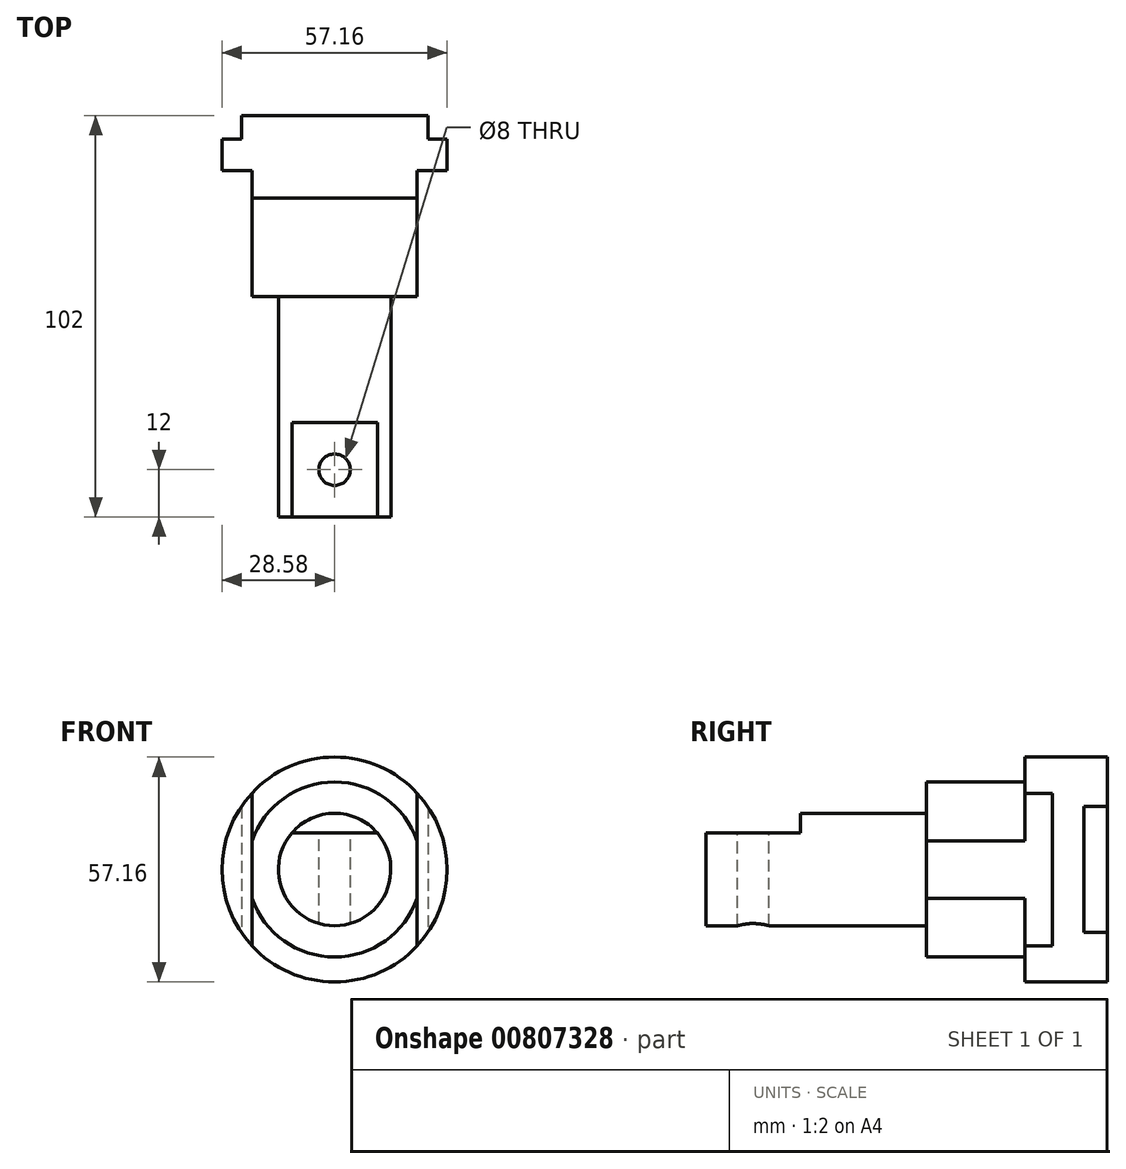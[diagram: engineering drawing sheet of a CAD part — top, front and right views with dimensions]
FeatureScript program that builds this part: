
annotation { "Feature Type Name" : "Feature", "Feature Type Description" : "" }
export const myFeature = defineFeature(function(context is Context, id is Id, definition is map)
    precondition{}
    {
        {
            var Q0;
            Q0=qCreatedBy(makeId("Front.planeOp"),FACE);
            var sketch = newSketch(context, id + "F0", { "sketchPlane" : qUnion([Q0])});
            skCircle(sketch, "E0", {"center": v(0, 0) * mm, "radius": 28.57 * mm});
            skCircle(sketch, "E1", {"center": v(0, 0) * mm, "radius": 22.23 * mm});
            skCircle(sketch, "E2", {"center": v(0, 0) * mm, "radius": 14.29 * mm});
            skLineSegment(sketch, "E3", {"start": v(-23.68, 16) * mm, "end": v(-23.68, -16) * mm});
            skLineSegment(sketch, "E4", {"start": v(0, 28.57) * mm, "end": v(0, -28.57) * mm, "construction": true});
            skLineSegment(sketch, "E5", {"start": v(28.57, 0) * mm, "end": v(-28.57, 0) * mm, "construction": true});
            skPoint(sketch, "E5.endSnap0", {"position": v(-23.68, 0) * mm});
            skLineSegment(sketch, "E6", {"start": v(-21, 19.38) * mm, "end": v(-21, -19.38) * mm});
            skLineSegment(sketch, "E7", {"start": v(-10.86, 9.29) * mm, "end": v(10.86, 9.29) * mm});
            skLineSegment(sketch, "E8.MirrorCS", {"start": v(23.68, 16) * mm, "end": v(23.68, -16) * mm});
            skLineSegment(sketch, "E9.MirrorCS", {"start": v(21, 19.38) * mm, "end": v(21, -19.38) * mm});
            skSolve(sketch);
        }
        {
            var Q0;
            {var subQ0=sQuery(id+"F0.wireOp",EDGE,"E3");Q0=makeQuery(id+"F0.imprint","IMPRINT",FACE,{"disambiguationData":[TD([[makeQuery(id+"F0.imprint","IMPRINT",EDGE,{"derivedFrom":subQ0}),1.0]])]});}
            var Q1;
            {var subQ0=sQuery(id+"F0.wireOp",EDGE,"E6");var subQ1=sQuery(id+"F0.wireOp",EDGE,"E1");var subQ2=makeQuery(id+"F0.imprint","INTERSECT",VERTEX,{"disambiguationData":[OD(0.0)],"derivedFrom":[subQ1,subQ0]});Q1=makeQuery(id+"F0.imprint","IMPRINT",FACE,{"disambiguationData":[TD([[makeQuery(id+"F0.imprint","IMPRINT",EDGE,{"disambiguationData":[TD([[subQ2,-1.0]])],"derivedFrom":subQ1}),1.0]])]});}
            var Q2;
            {var subQ0=sQuery(id+"F0.wireOp",EDGE,"E6");var subQ1=sQuery(id+"F0.wireOp",EDGE,"E0");var subQ2=makeQuery(id+"F0.imprint","INTERSECT",VERTEX,{"disambiguationData":[OD(0.0)],"derivedFrom":[subQ1,subQ0]});Q2=makeQuery(id+"F0.imprint","IMPRINT",FACE,{"disambiguationData":[TD([[makeQuery(id+"F0.imprint","IMPRINT",EDGE,{"disambiguationData":[TD([[subQ2,1.0]])],"derivedFrom":subQ1}),1.0]])]});}
            var Q3;
            {var subQ4=sQuery(id+"F0.wireOp",EDGE,"E6");var subQ5=sQuery(id+"F0.wireOp",EDGE,"E1");var subQ10=makeQuery(id+"F0.imprint","INTERSECT",VERTEX,{"disambiguationData":[OD(0.0)],"derivedFrom":[subQ5,subQ4]});Q3=makeQuery(id+"F0.imprint","IMPRINT",FACE,{"disambiguationData":[TD([[makeQuery(id+"F0.imprint","IMPRINT",EDGE,{"disambiguationData":[TD([[subQ10,1.0]])],"derivedFrom":subQ5}),1.0]])]});}
            var Q4;
            {var subQ0=sQuery(id+"F0.wireOp",EDGE,"E6");var subQ1=sQuery(id+"F0.wireOp",EDGE,"E0");var subQ2=makeQuery(id+"F0.imprint","INTERSECT",VERTEX,{"disambiguationData":[OD(1.0)],"derivedFrom":[subQ1,subQ0]});Q4=makeQuery(id+"F0.imprint","IMPRINT",FACE,{"disambiguationData":[TD([[makeQuery(id+"F0.imprint","IMPRINT",EDGE,{"disambiguationData":[TD([[subQ2,-1.0]])],"derivedFrom":subQ1}),1.0]])]});}
            var Q5;
            {var subQ0=sQuery(id+"F0.wireOp",EDGE,"E9.MirrorCS");var subQ1=sQuery(id+"F0.wireOp",EDGE,"E1");var subQ2=makeQuery(id+"F0.imprint","INTERSECT",VERTEX,{"disambiguationData":[OD(0.0)],"derivedFrom":[subQ1,subQ0]});Q5=makeQuery(id+"F0.imprint","IMPRINT",FACE,{"disambiguationData":[TD([[makeQuery(id+"F0.imprint","IMPRINT",EDGE,{"disambiguationData":[TD([[subQ2,1.0]])],"derivedFrom":subQ1}),1.0]])]});}
            var Q6;
            {var subQ0=sQuery(id+"F0.wireOp",EDGE,"E8.MirrorCS");Q6=makeQuery(id+"F0.imprint","IMPRINT",FACE,{"disambiguationData":[TD([[makeQuery(id+"F0.imprint","IMPRINT",EDGE,{"derivedFrom":subQ0}),-1.0]])]});}
            var Q7;
            {var subQ0=sQuery(id+"F0.wireOp",EDGE,"E7");Q7=makeQuery(id+"F0.imprint","IMPRINT",FACE,{"disambiguationData":[TD([[makeQuery(id+"F0.imprint","IMPRINT",EDGE,{"derivedFrom":subQ0}),-1.0]])]});}
            var Q8;
            {var subQ0=sQuery(id+"F0.wireOp",EDGE,"E7");Q8=makeQuery(id+"F0.imprint","IMPRINT",FACE,{"disambiguationData":[TD([[makeQuery(id+"F0.imprint","IMPRINT",EDGE,{"derivedFrom":subQ0}),1.0]])]});}
            extrude(context, id + "F1", {"entities" : qUnion([Q0, Q1, Q2, Q3, Q4, Q5, Q6, Q7, Q8]), "oppositeDirection" : true, "depth" : 6 * mm, "offsetDistance" : 25 * mm});
        }
        {
            var Q0;
            {var subQ0=sQuery(id+"F0.wireOp",EDGE,"E7");Q0=makeQuery(id+"F0.imprint","IMPRINT",FACE,{"disambiguationData":[TD([[makeQuery(id+"F0.imprint","IMPRINT",EDGE,{"derivedFrom":subQ0}),-1.0]])]});}
            var Q1;
            {var subQ0=sQuery(id+"F0.wireOp",EDGE,"E6");var subQ1=sQuery(id+"F0.wireOp",EDGE,"E1");var subQ2=makeQuery(id+"F0.imprint","INTERSECT",VERTEX,{"disambiguationData":[OD(0.0)],"derivedFrom":[subQ1,subQ0]});Q1=makeQuery(id+"F0.imprint","IMPRINT",FACE,{"disambiguationData":[TD([[makeQuery(id+"F0.imprint","IMPRINT",EDGE,{"disambiguationData":[TD([[subQ2,-1.0]])],"derivedFrom":subQ1}),1.0]])]});}
            var Q2;
            {var subQ0=sQuery(id+"F0.wireOp",EDGE,"E7");Q2=makeQuery(id+"F0.imprint","IMPRINT",FACE,{"disambiguationData":[TD([[makeQuery(id+"F0.imprint","IMPRINT",EDGE,{"derivedFrom":subQ0}),1.0]])]});}
            var Q3;
            {var subQ0=sQuery(id+"F0.wireOp",EDGE,"E9.MirrorCS");var subQ1=sQuery(id+"F0.wireOp",EDGE,"E1");var subQ2=makeQuery(id+"F0.imprint","INTERSECT",VERTEX,{"disambiguationData":[OD(0.0)],"derivedFrom":[subQ1,subQ0]});Q3=makeQuery(id+"F0.imprint","IMPRINT",FACE,{"disambiguationData":[TD([[makeQuery(id+"F0.imprint","IMPRINT",EDGE,{"disambiguationData":[TD([[subQ2,1.0]])],"derivedFrom":subQ1}),1.0]])]});}
            var Q4;
            {var subQ0=sQuery(id+"F0.wireOp",EDGE,"E6");var subQ1=sQuery(id+"F0.wireOp",EDGE,"E0");var subQ2=makeQuery(id+"F0.imprint","INTERSECT",VERTEX,{"disambiguationData":[OD(0.0)],"derivedFrom":[subQ1,subQ0]});Q4=makeQuery(id+"F0.imprint","IMPRINT",FACE,{"disambiguationData":[TD([[makeQuery(id+"F0.imprint","IMPRINT",EDGE,{"disambiguationData":[TD([[subQ2,1.0]])],"derivedFrom":subQ1}),1.0]])]});}
            var Q5;
            {var subQ0=sQuery(id+"F0.wireOp",EDGE,"E8.MirrorCS");Q5=makeQuery(id+"F0.imprint","IMPRINT",FACE,{"disambiguationData":[TD([[makeQuery(id+"F0.imprint","IMPRINT",EDGE,{"derivedFrom":subQ0}),1.0]])]});}
            var Q6;
            {var subQ0=sQuery(id+"F0.wireOp",EDGE,"E3");Q6=makeQuery(id+"F0.imprint","IMPRINT",FACE,{"disambiguationData":[TD([[makeQuery(id+"F0.imprint","IMPRINT",EDGE,{"derivedFrom":subQ0}),-1.0]])]});}
            var Q7;
            {var subQ0=sQuery(id+"F0.wireOp",EDGE,"E6");var subQ1=sQuery(id+"F0.wireOp",EDGE,"E0");var subQ2=makeQuery(id+"F0.imprint","INTERSECT",VERTEX,{"disambiguationData":[OD(1.0)],"derivedFrom":[subQ1,subQ0]});Q7=makeQuery(id+"F0.imprint","IMPRINT",FACE,{"disambiguationData":[TD([[makeQuery(id+"F0.imprint","IMPRINT",EDGE,{"disambiguationData":[TD([[subQ2,-1.0]])],"derivedFrom":subQ1}),1.0]])]});}
            var Q8;
            {var subQ0=sQuery(id+"F0.wireOp",EDGE,"E8.MirrorCS");Q8=makeQuery(id+"F0.imprint","IMPRINT",FACE,{"disambiguationData":[TD([[makeQuery(id+"F0.imprint","IMPRINT",EDGE,{"derivedFrom":subQ0}),-1.0]])]});}
            var Q9;
            {var subQ0=sQuery(id+"F0.wireOp",EDGE,"E3");Q9=makeQuery(id+"F0.imprint","IMPRINT",FACE,{"disambiguationData":[TD([[makeQuery(id+"F0.imprint","IMPRINT",EDGE,{"derivedFrom":subQ0}),1.0]])]});}
            var Q10;
            {var subQ4=sQuery(id+"F0.wireOp",EDGE,"E6");var subQ5=sQuery(id+"F0.wireOp",EDGE,"E1");var subQ10=makeQuery(id+"F0.imprint","INTERSECT",VERTEX,{"disambiguationData":[OD(0.0)],"derivedFrom":[subQ5,subQ4]});Q10=makeQuery(id+"F0.imprint","IMPRINT",FACE,{"disambiguationData":[TD([[makeQuery(id+"F0.imprint","IMPRINT",EDGE,{"disambiguationData":[TD([[subQ10,1.0]])],"derivedFrom":subQ5}),1.0]])]});}
            extrude(context, id + "F2", {"entities" : qUnion([Q0, Q1, Q2, Q3, Q4, Q5, Q6, Q7, Q8, Q9, Q10]), "operationType" : NewBodyOperationType.ADD, "depth" : (46 - 32 - 6) * mm, "offsetDistance" : 25 * mm});
        }
        {
            var Q0;
            {var subQ0=sQuery(id+"F0.wireOp",EDGE,"E7");Q0=makeQuery(id+"F0.imprint","IMPRINT",FACE,{"disambiguationData":[TD([[makeQuery(id+"F0.imprint","IMPRINT",EDGE,{"derivedFrom":subQ0}),-1.0]])]});}
            var Q1;
            {var subQ0=sQuery(id+"F0.wireOp",EDGE,"E7");Q1=makeQuery(id+"F0.imprint","IMPRINT",FACE,{"disambiguationData":[TD([[makeQuery(id+"F0.imprint","IMPRINT",EDGE,{"derivedFrom":subQ0}),1.0]])]});}
            var Q2;
            {var subQ4=sQuery(id+"F0.wireOp",EDGE,"E6");var subQ5=sQuery(id+"F0.wireOp",EDGE,"E1");var subQ10=makeQuery(id+"F0.imprint","INTERSECT",VERTEX,{"disambiguationData":[OD(0.0)],"derivedFrom":[subQ5,subQ4]});Q2=makeQuery(id+"F0.imprint","IMPRINT",FACE,{"disambiguationData":[TD([[makeQuery(id+"F0.imprint","IMPRINT",EDGE,{"disambiguationData":[TD([[subQ10,1.0]])],"derivedFrom":subQ5}),1.0]])]});}
            var Q3;
            {var subQ0=sQuery(id+"F0.wireOp",EDGE,"E6");var subQ1=sQuery(id+"F0.wireOp",EDGE,"E0");var subQ2=makeQuery(id+"F0.imprint","INTERSECT",VERTEX,{"disambiguationData":[OD(0.0)],"derivedFrom":[subQ1,subQ0]});Q3=makeQuery(id+"F0.imprint","IMPRINT",FACE,{"disambiguationData":[TD([[makeQuery(id+"F0.imprint","IMPRINT",EDGE,{"disambiguationData":[TD([[subQ2,1.0]])],"derivedFrom":subQ1}),1.0]])]});}
            var Q4;
            {var subQ0=sQuery(id+"F0.wireOp",EDGE,"E6");var subQ1=sQuery(id+"F0.wireOp",EDGE,"E0");var subQ2=makeQuery(id+"F0.imprint","INTERSECT",VERTEX,{"disambiguationData":[OD(1.0)],"derivedFrom":[subQ1,subQ0]});Q4=makeQuery(id+"F0.imprint","IMPRINT",FACE,{"disambiguationData":[TD([[makeQuery(id+"F0.imprint","IMPRINT",EDGE,{"disambiguationData":[TD([[subQ2,-1.0]])],"derivedFrom":subQ1}),1.0]])]});}
            extrude(context, id + "F3", {"entities" : qUnion([Q0, Q1, Q2, Q3, Q4]), "operationType" : NewBodyOperationType.ADD, "depth" : 15 * mm, "offsetDistance" : 25 * mm});
        }
        {
            var Q0;
            {var subQ0=sQuery(id+"F0.wireOp",EDGE,"E7");Q0=makeQuery(id+"F0.imprint","IMPRINT",FACE,{"disambiguationData":[TD([[makeQuery(id+"F0.imprint","IMPRINT",EDGE,{"derivedFrom":subQ0}),-1.0]])]});}
            var Q1;
            {var subQ0=sQuery(id+"F0.wireOp",EDGE,"E7");Q1=makeQuery(id+"F0.imprint","IMPRINT",FACE,{"disambiguationData":[TD([[makeQuery(id+"F0.imprint","IMPRINT",EDGE,{"derivedFrom":subQ0}),1.0]])]});}
            extrude(context, id + "F4", {"entities" : qUnion([Q0, Q1]), "operationType" : NewBodyOperationType.ADD, "depth" : (102 - 30) * mm, "offsetDistance" : 25 * mm});
        }
        {
            var Q0;
            {var subQ0=sQuery(id+"F0.wireOp",EDGE,"E7");Q0=makeQuery(id+"F0.imprint","IMPRINT",FACE,{"disambiguationData":[TD([[makeQuery(id+"F0.imprint","IMPRINT",EDGE,{"derivedFrom":subQ0}),-1.0]])]});}
            extrude(context, id + "F5", {"entities" : qUnion([Q0]), "operationType" : NewBodyOperationType.ADD, "depth" : (102 - 6) * mm, "offsetDistance" : 25 * mm});
        }
        {
            var Q0;
            {var subQ4=sQuery(id+"F0.wireOp",EDGE,"E6");var subQ5=sQuery(id+"F0.wireOp",EDGE,"E1");var subQ10=makeQuery(id+"F0.imprint","INTERSECT",VERTEX,{"disambiguationData":[OD(0.0)],"derivedFrom":[subQ5,subQ4]});Q0=makeQuery(id+"F0.imprint","IMPRINT",FACE,{"disambiguationData":[TD([[makeQuery(id+"F0.imprint","IMPRINT",EDGE,{"disambiguationData":[TD([[subQ10,1.0]])],"derivedFrom":subQ5}),1.0]])]});}
            var Q1;
            {var subQ0=sQuery(id+"F0.wireOp",EDGE,"E7");Q1=makeQuery(id+"F0.imprint","IMPRINT",FACE,{"disambiguationData":[TD([[makeQuery(id+"F0.imprint","IMPRINT",EDGE,{"derivedFrom":subQ0}),-1.0]])]});}
            var Q2;
            {var subQ0=sQuery(id+"F0.wireOp",EDGE,"E7");Q2=makeQuery(id+"F0.imprint","IMPRINT",FACE,{"disambiguationData":[TD([[makeQuery(id+"F0.imprint","IMPRINT",EDGE,{"derivedFrom":subQ0}),1.0]])]});}
            extrude(context, id + "F6", {"entities" : qUnion([Q0, Q1, Q2]), "operationType" : NewBodyOperationType.ADD, "depth" : 40 * mm, "offsetDistance" : 25 * mm});
        }
        {
            var Q0;
            Q0=makeQuery(id+"F5.opExtrude","SWEPT_FACE",FACE,{"disambiguationData":[OSD([sQuery(id+"F0.wireOp",EDGE,"E7")])]});
            var sketch = newSketch(context, id + "F7", { "sketchPlane" : qUnion([Q0])});
            skLineSegment(sketch, "E10.0.0", {"start": v(10.86, -96) * mm, "end": v(10.86, -72) * mm});
            skLineSegment(sketch, "E10.0.1", {"start": v(10.86, -72) * mm, "end": v(-10.86, -72) * mm});
            skLineSegment(sketch, "E10.0.2", {"start": v(-10.86, -72) * mm, "end": v(-10.86, -96) * mm});
            skLineSegment(sketch, "E10.0.3", {"start": v(-10.86, -96) * mm, "end": v(10.86, -96) * mm});
            skLineSegment(sketch, "E11", {"start": v(0, -96) * mm, "end": v(0, -72) * mm, "construction": true});
            skCircle(sketch, "E12", {"center": v(0, -84) * mm, "radius": 4 * mm});
            skSolve(sketch);
        }
        {
            var Q0;
            Q0=makeQuery(id+"F7.imprint","IMPRINT",FACE,{"disambiguationData":[TD([[makeQuery(id+"F7.imprint","IMPRINT",EDGE,{"derivedFrom":sQuery(id+"F7.wireOp",EDGE,"E12")}),1.0]])]});
            extrude(context, id + "F8", {"entities" : qUnion([Q0]), "operationType" : NewBodyOperationType.REMOVE, "oppositeDirection" : true, "depth" : 25 * mm, "offsetDistance" : 25 * mm});
        }
    });
